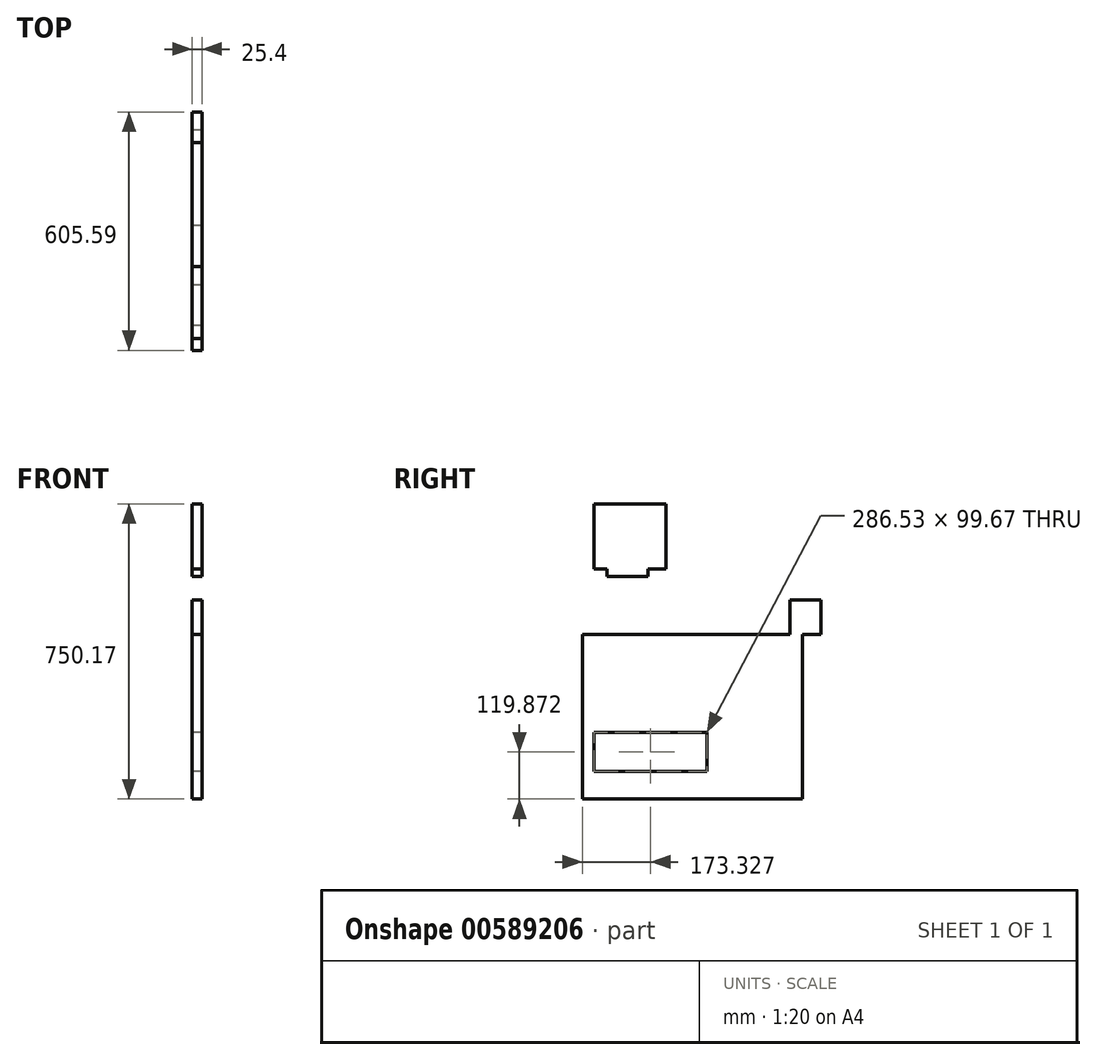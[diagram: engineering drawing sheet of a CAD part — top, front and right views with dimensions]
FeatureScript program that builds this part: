
annotation { "Feature Type Name" : "Feature", "Feature Type Description" : "" }
export const myFeature = defineFeature(function(context is Context, id is Id, definition is map)
    precondition{}
    {
        {
            var Q0;
            Q0=qCreatedBy(makeId("Right.planeOp"),FACE);
            var sketch = newSketch(context, id + "F0", { "sketchPlane" : qUnion([Q0])});
            skLineSegment(sketch, "E0.bottom", {"start": v(-287.8, 96.53) * mm, "end": v(-184.2, 96.53) * mm});
            skLineSegment(sketch, "E0.top", {"start": v(-287.8, -18.37) * mm, "end": v(-184.2, -18.37) * mm});
            skLineSegment(sketch, "E0.left", {"start": v(-287.8, 96.53) * mm, "end": v(-287.8, -18.37) * mm});
            skLineSegment(sketch, "E0.right", {"start": v(-184.2, 96.53) * mm, "end": v(-184.2, -18.37) * mm});
            skLineSegment(sketch, "E1.bottom", {"start": v(-184.2, 96.53) * mm, "end": v(-184.2, 96.53) * mm});
            skLineSegment(sketch, "E1.top", {"start": v(-184.2, 329.33) * mm, "end": v(-184.2, 329.33) * mm});
            skLineSegment(sketch, "E1.left", {"start": v(-184.2, 96.53) * mm, "end": v(-184.2, 329.33) * mm});
            skLineSegment(sketch, "E1.right", {"start": v(-184.2, 96.53) * mm, "end": v(-184.2, 329.33) * mm});
            skLineSegment(sketch, "E2.bottom", {"start": v(-184.2, -18.37) * mm, "end": v(-184.2, -18.37) * mm});
            skLineSegment(sketch, "E2.top", {"start": v(-184.2, 259.09) * mm, "end": v(-184.2, 259.09) * mm});
            skLineSegment(sketch, "E2.left", {"start": v(-184.2, -18.37) * mm, "end": v(-184.2, 259.09) * mm});
            skLineSegment(sketch, "E2.right", {"start": v(-184.2, -18.37) * mm, "end": v(-184.2, 259.09) * mm});
            skLineSegment(sketch, "E3.bottom", {"start": v(-137.89, 0) * mm, "end": v(-320.5, 0) * mm});
            skLineSegment(sketch, "E3.top", {"start": v(-137.89, 166.03) * mm, "end": v(-320.5, 166.03) * mm});
            skLineSegment(sketch, "E3.left", {"start": v(-137.89, 0) * mm, "end": v(-137.89, 166.03) * mm});
            skLineSegment(sketch, "E3.right", {"start": v(-320.5, 0) * mm, "end": v(-320.5, 166.03) * mm});
            skLineSegment(sketch, "E4.bottom", {"start": v(255.02, -77.84) * mm, "end": v(176.75, -77.84) * mm});
            skLineSegment(sketch, "E4.top", {"start": v(255.02, -166.48) * mm, "end": v(176.75, -166.48) * mm});
            skLineSegment(sketch, "E4.left", {"start": v(255.02, -77.84) * mm, "end": v(255.02, -166.48) * mm});
            skLineSegment(sketch, "E4.right", {"start": v(176.75, -77.84) * mm, "end": v(176.75, -166.48) * mm});
            skLineSegment(sketch, "E5.bottom", {"start": v(-350.57, -584.14) * mm, "end": v(208.98, -584.14) * mm});
            skLineSegment(sketch, "E5.top", {"start": v(-350.57, -166.48) * mm, "end": v(208.98, -166.48) * mm});
            skLineSegment(sketch, "E5.left", {"start": v(-350.57, -584.14) * mm, "end": v(-350.57, -166.48) * mm});
            skLineSegment(sketch, "E5.right", {"start": v(208.98, -584.14) * mm, "end": v(208.98, -166.48) * mm});
            skLineSegment(sketch, "E6.bottom", {"start": v(-33.98, -514.1) * mm, "end": v(-320.5, -514.1) * mm});
            skLineSegment(sketch, "E6.top", {"start": v(-33.98, -414.43) * mm, "end": v(-320.5, -414.43) * mm});
            skLineSegment(sketch, "E6.left", {"start": v(-33.98, -514.1) * mm, "end": v(-33.98, -414.43) * mm});
            skLineSegment(sketch, "E6.right", {"start": v(-320.5, -514.1) * mm, "end": v(-320.5, -414.43) * mm});
            skSolve(sketch);
        }
        {
            var Q0;
            Q0 = qSketchRegion(id + "F0", true);
            extrude(context, id + "F1", {"entities" : qUnion([Q0]), "depth" : 25.4 * mm, "offsetDistance" : 25.4 * mm});
        }
    });
